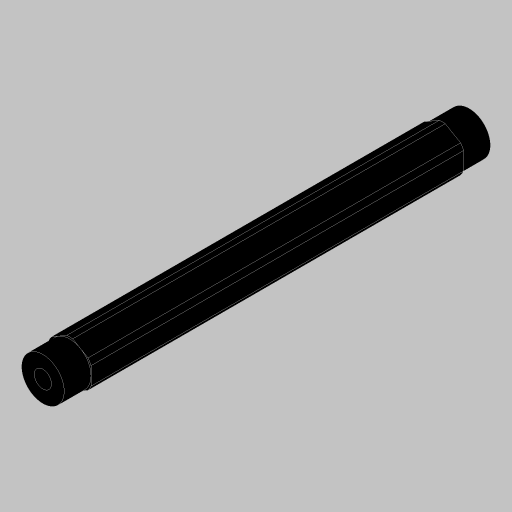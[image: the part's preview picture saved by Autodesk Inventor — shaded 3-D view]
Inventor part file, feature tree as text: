
AUTODESK INVENTOR PART (.ipt)
format: ipt  version: 2023.5 (Build 275446000, 446)  size: 165,376 bytes
history: native  units: in
note: dims shown in document units (in); Inventor stores cm internally (conversion verified against a paired STEP export)
features: extrude x3, projected_geometry x3, hole x1, mirror x1, sketch x1
ambient origin geometry x8: Origin, YZ Plane, XZ Plane, XY Plane, X Axis, Y Axis, Z Axis, Center Point
bodies: Solid1 (feature_tree)
feature tree (9):
  extrude  "Extrusion1"  Depth=0.315in
  hole  "Hole1"  [1 undecoded]
  extrude  "Extrusion3"  Depth=0.5in
  extrude  "Extrusion4"  Depth=0.315in TaperAngle=0.0deg
  mirror  "Mirror2"
  sketch  "Sketch5"  dims[d2=0.0in d9=0.625in d10=0.385in d11=0.25in d12=0.5635in d13=1.0in d14=0.8108in d16=0.7in d17=0.0in d18=0.0in d19=0.5in d20=0.315in d21=0.0in]
  projected_geometry  "Projected Loop2"
  projected_geometry  "Project Cut Edges1"
  projected_geometry  "Project Cut Edges2"
note: 1 required parameter value undecoded (feature->parameter linkage not recoverable at this tier; creation-order binding heuristic only, values carry confidence <= 0.55)
